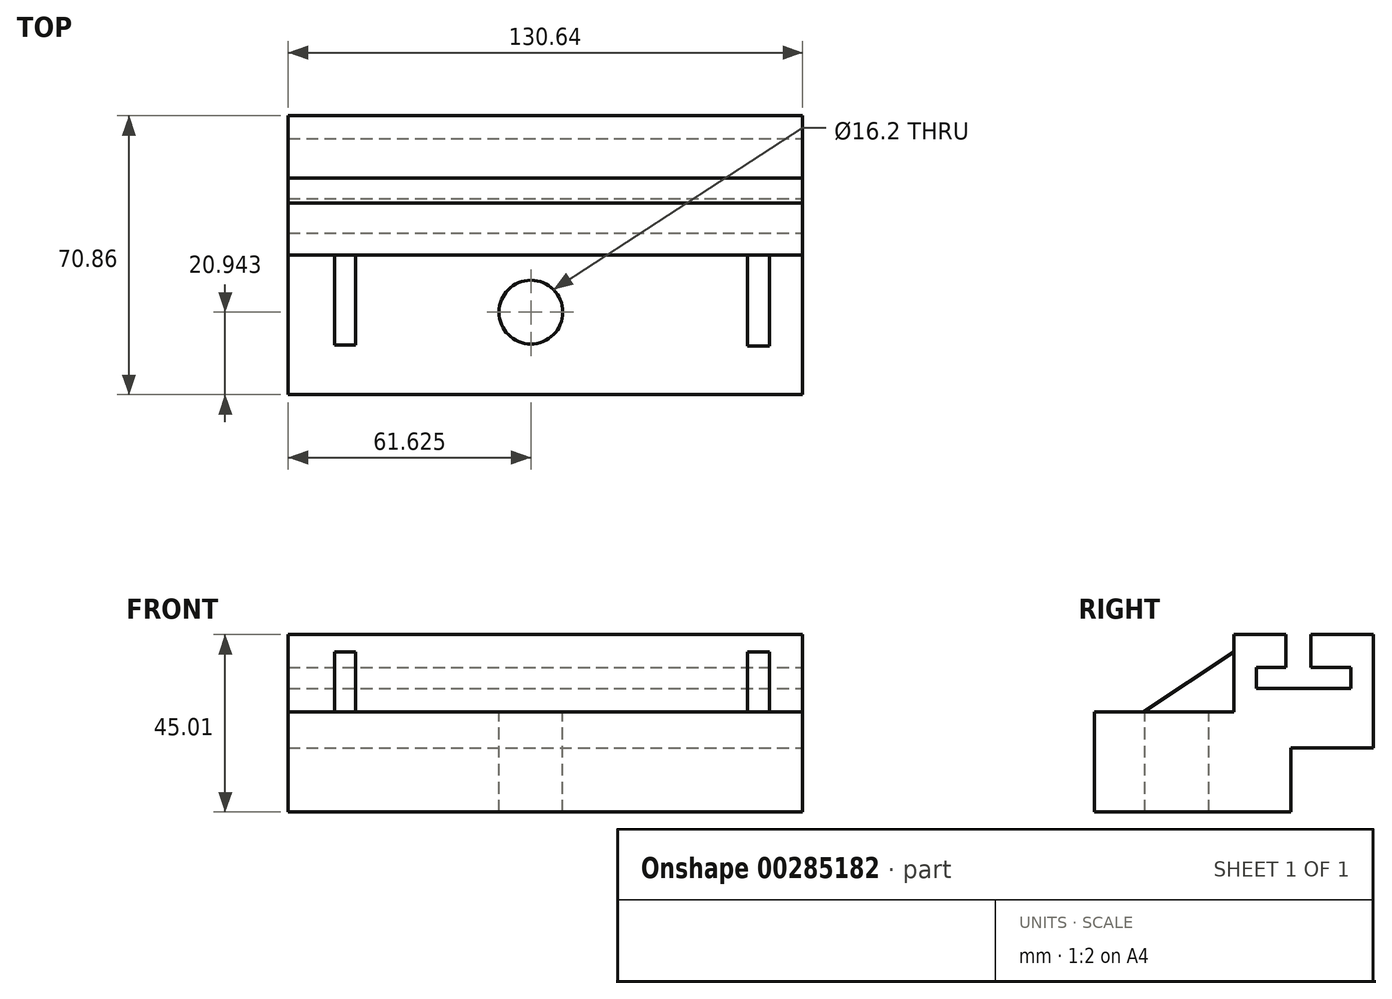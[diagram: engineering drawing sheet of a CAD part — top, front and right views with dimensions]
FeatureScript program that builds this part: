
annotation { "Feature Type Name" : "Feature", "Feature Type Description" : "" }
export const myFeature = defineFeature(function(context is Context, id is Id, definition is map)
    precondition{}
    {
        {
            var Q0;
            Q0=qCreatedBy(makeId("Top.planeOp"),FACE);
            var sketch = newSketch(context, id + "F0", { "sketchPlane" : qUnion([Q0])});
            skLineSegment(sketch, "E0.bottom", {"start": v(-58.77, 27.96) * mm, "end": v(71.87, 27.96) * mm});
            skLineSegment(sketch, "E0.top", {"start": v(-58.77, -42.9) * mm, "end": v(71.87, -42.9) * mm});
            skLineSegment(sketch, "E0.left", {"start": v(-58.77, 27.96) * mm, "end": v(-58.77, -42.9) * mm});
            skLineSegment(sketch, "E0.right", {"start": v(71.87, 27.96) * mm, "end": v(71.87, -42.9) * mm});
            skSolve(sketch);
        }
        {
            var Q0;
            Q0=makeQuery(id+"F0.imprint","IMPRINT",FACE,{"disambiguationData":[TD([[makeQuery(id+"F0.imprint","IMPRINT",EDGE,{"derivedFrom":sQuery(id+"F0.wireOp",EDGE,"E0.bottom")}),-1.0]])]});
            extrude(context, id + "F1", {"entities" : qUnion([Q0]), "depth" : 25.4 * mm});
        }
        {
            var Q0;
            Q0=makeQuery(id+"F1.opExtrude","SWEPT_FACE",FACE,{"disambiguationData":[OSD([sQuery(id+"F0.wireOp",EDGE,"E0.right")])]});
            var sketch = newSketch(context, id + "F2", { "sketchPlane" : qUnion([Q0])});
            skLineSegment(sketch, "E1.bottom", {"start": v(6.95, 0) * mm, "end": v(27.96, 0) * mm});
            skLineSegment(sketch, "E1.top", {"start": v(6.95, 16.2) * mm, "end": v(27.96, 16.2) * mm});
            skLineSegment(sketch, "E1.left", {"start": v(6.95, 0) * mm, "end": v(6.95, 16.2) * mm});
            skLineSegment(sketch, "E1.right", {"start": v(27.96, 0) * mm, "end": v(27.96, 16.2) * mm});
            skSolve(sketch);
        }
        {
            var Q0;
            Q0=makeQuery(id+"F2.imprint","IMPRINT",FACE,{"disambiguationData":[TD([[makeQuery(id+"F2.imprint","IMPRINT",EDGE,{"derivedFrom":sQuery(id+"F2.wireOp",EDGE,"E1.bottom")}),-1.0]])]});
            extrude(context, id + "F3", {"entities" : qUnion([Q0]), "operationType" : NewBodyOperationType.REMOVE, "oppositeDirection" : true, "depth" : 139.7 * mm});
        }
        {
            var Q0;
            Q0=makeQuery(id+"F1.opExtrude","CAP_FACE",FACE,{"disambiguationData":[OSD([sQuery(id+"F0.wireOp",EDGE,"E0.bottom"),sQuery(id+"F0.wireOp",EDGE,"E0.top"),sQuery(id+"F0.wireOp",EDGE,"E0.left"),sQuery(id+"F0.wireOp",EDGE,"E0.right")])],"isStart":false});
            var sketch = newSketch(context, id + "F4", { "sketchPlane" : qUnion([Q0])});
            skLineSegment(sketch, "E2.bottom", {"start": v(-58.77, 27.96) * mm, "end": v(71.87, 27.96) * mm});
            skLineSegment(sketch, "E2.top", {"start": v(-58.77, -7.47) * mm, "end": v(71.87, -7.47) * mm});
            skLineSegment(sketch, "E2.left", {"start": v(-58.77, 27.96) * mm, "end": v(-58.77, -7.47) * mm});
            skLineSegment(sketch, "E2.right", {"start": v(71.87, 27.96) * mm, "end": v(71.87, -7.47) * mm});
            skSolve(sketch);
        }
        {
            var Q0;
            Q0=makeQuery(id+"F4.imprint","IMPRINT",FACE,{"disambiguationData":[TD([[makeQuery(id+"F4.imprint","IMPRINT",EDGE,{"derivedFrom":sQuery(id+"F4.wireOp",EDGE,"E2.bottom")}),-1.0]])]});
            extrude(context, id + "F5", {"entities" : qUnion([Q0]), "operationType" : NewBodyOperationType.ADD, "depth" : 27.94 * mm});
        }
        {
            var Q0;
            Q0=makeQuery(id+"F5.boolean.opBoolean","MERGE",FACE,{"derivedFrom":[makeQuery(id+"F1.opExtrude","SWEPT_FACE",FACE,{"disambiguationData":[OSD([sQuery(id+"F0.wireOp",EDGE,"E0.right")])]}),makeQuery(id+"F5.opExtrude","SWEPT_FACE",FACE,{"disambiguationData":[OSD([sQuery(id+"F4.wireOp",EDGE,"E2.right")])]})]});
            var sketch = newSketch(context, id + "F6", { "sketchPlane" : qUnion([Q0])});
            skLineSegment(sketch, "E3", {"start": v(5.7, 53.34) * mm, "end": v(5.7, 36.69) * mm});
            skLineSegment(sketch, "E4", {"start": v(5.7, 36.69) * mm, "end": v(-1.85, 36.69) * mm});
            skLineSegment(sketch, "E5", {"start": v(-1.85, 36.69) * mm, "end": v(-1.85, 31.32) * mm});
            skLineSegment(sketch, "E6", {"start": v(-1.85, 31.32) * mm, "end": v(22.16, 31.32) * mm});
            skLineSegment(sketch, "E7", {"start": v(22.16, 36.69) * mm, "end": v(22.16, 31.32) * mm});
            skLineSegment(sketch, "E8", {"start": v(22.16, 36.69) * mm, "end": v(12.09, 36.69) * mm});
            skLineSegment(sketch, "E9", {"start": v(12.09, 36.69) * mm, "end": v(12.09, 53.34) * mm});
            skSolve(sketch);
        }
        {
            var Q0;
            {var subQ0=sQuery(id+"F6.wireOp",EDGE,"E3");Q0=makeQuery(id+"F6.imprint","IMPRINT",FACE,{"disambiguationData":[TD([[makeQuery(id+"F6.imprint","IMPRINT",EDGE,{"derivedFrom":subQ0}),1.0]])]});}
            extrude(context, id + "F7", {"entities" : qUnion([Q0]), "operationType" : NewBodyOperationType.REMOVE, "oppositeDirection" : true, "depth" : 157.48 * mm});
        }
        {
            var Q0;
            Q0=makeQuery(id+"F5.boolean.opBoolean","MERGE",FACE,{"derivedFrom":[makeQuery(id+"F1.opExtrude","SWEPT_FACE",FACE,{"disambiguationData":[OSD([sQuery(id+"F0.wireOp",EDGE,"E0.right")])]}),makeQuery(id+"F5.opExtrude","SWEPT_FACE",FACE,{"disambiguationData":[OSD([sQuery(id+"F4.wireOp",EDGE,"E2.right")])]})]});
            var sketch = newSketch(context, id + "F8", { "sketchPlane" : qUnion([Q0])});
            skLineSegment(sketch, "E10.bottom", {"start": v(-7.47, 53.34) * mm, "end": v(5.7, 53.34) * mm});
            skLineSegment(sketch, "E10.top", {"start": v(-7.47, 45.01) * mm, "end": v(5.7, 45.01) * mm});
            skLineSegment(sketch, "E10.left", {"start": v(-7.47, 53.34) * mm, "end": v(-7.47, 45.01) * mm});
            skLineSegment(sketch, "E10.right", {"start": v(5.7, 53.34) * mm, "end": v(5.7, 45.01) * mm});
            skPoint(sketch, "E11.oppositeSnap0", {"position": v(12.09, 45.01) * mm});
            skLineSegment(sketch, "E11.bottom", {"start": v(12.09, 53.34) * mm, "end": v(27.96, 53.34) * mm});
            skLineSegment(sketch, "E11.top", {"start": v(12.09, 45.01) * mm, "end": v(27.96, 45.01) * mm});
            skLineSegment(sketch, "E11.left", {"start": v(12.09, 53.34) * mm, "end": v(12.09, 45.01) * mm});
            skLineSegment(sketch, "E11.right", {"start": v(27.96, 53.34) * mm, "end": v(27.96, 45.01) * mm});
            skSolve(sketch);
        }
        {
            var Q0;
            Q0=makeQuery(id+"F8.imprint","IMPRINT",FACE,{"disambiguationData":[TD([[makeQuery(id+"F8.imprint","IMPRINT",EDGE,{"derivedFrom":sQuery(id+"F8.wireOp",EDGE,"E10.bottom")}),1.0]])]});
            var Q1;
            Q1=makeQuery(id+"F8.imprint","IMPRINT",FACE,{"disambiguationData":[TD([[makeQuery(id+"F8.imprint","IMPRINT",EDGE,{"derivedFrom":sQuery(id+"F8.wireOp",EDGE,"E11.bottom")}),1.0]])]});
            extrude(context, id + "F9", {"entities" : qUnion([Q0, Q1]), "operationType" : NewBodyOperationType.REMOVE, "oppositeDirection" : true, "depth" : 147.32 * mm});
        }
        {
            var Q0;
            Q0=makeQuery(id+"F1.opExtrude","CAP_FACE",FACE,{"disambiguationData":[OSD([sQuery(id+"F0.wireOp",EDGE,"E0.bottom"),sQuery(id+"F0.wireOp",EDGE,"E0.top"),sQuery(id+"F0.wireOp",EDGE,"E0.left"),sQuery(id+"F0.wireOp",EDGE,"E0.right")])],"isStart":false});
            var sketch = newSketch(context, id + "F10", { "sketchPlane" : qUnion([Q0])});
            skLineSegment(sketch, "E12.bottom", {"start": v(-47.02, -7.47) * mm, "end": v(-41.64, -7.47) * mm});
            skLineSegment(sketch, "E12.top", {"start": v(-47.02, -30.27) * mm, "end": v(-41.64, -30.27) * mm});
            skLineSegment(sketch, "E12.left", {"start": v(-47.02, -7.47) * mm, "end": v(-47.02, -30.27) * mm});
            skLineSegment(sketch, "E12.right", {"start": v(-41.64, -7.47) * mm, "end": v(-41.64, -30.27) * mm});
            skSolve(sketch);
        }
        {
            var Q0;
            Q0=makeQuery(id+"F10.imprint","IMPRINT",FACE,{"disambiguationData":[TD([[makeQuery(id+"F10.imprint","IMPRINT",EDGE,{"derivedFrom":sQuery(id+"F10.wireOp",EDGE,"E12.bottom")}),-1.0]])]});
            extrude(context, id + "F11", {"entities" : qUnion([Q0]), "operationType" : NewBodyOperationType.ADD, "depth" : 15.24 * mm});
        }
        {
            var Q0;
            Q0=makeQuery(id+"F11.opExtrude","SWEPT_FACE",FACE,{"disambiguationData":[OSD([sQuery(id+"F10.wireOp",EDGE,"E12.left")])]});
            var sketch = newSketch(context, id + "F12", { "sketchPlane" : qUnion([Q0])});
            skLineSegment(sketch, "E13", {"start": v(7.47, 40.64) * mm, "end": v(30.27, 25.4) * mm});
            skSolve(sketch);
        }
        {
            var Q0;
            Q0=makeQuery(id+"F12.imprint","IMPRINT",FACE,{"disambiguationData":[TD([[makeQuery(id+"F12.imprint","IMPRINT",EDGE,{"derivedFrom":sQuery(id+"F12.wireOp",EDGE,"E13")}),1.0]])]});
            extrude(context, id + "F13", {"entities" : qUnion([Q0]), "operationType" : NewBodyOperationType.REMOVE, "oppositeDirection" : true, "depth" : 25.4 * mm});
        }
        {
            var Q0;
            Q0=makeQuery(id+"F1.opExtrude","CAP_FACE",FACE,{"disambiguationData":[OSD([sQuery(id+"F0.wireOp",EDGE,"E0.bottom"),sQuery(id+"F0.wireOp",EDGE,"E0.top"),sQuery(id+"F0.wireOp",EDGE,"E0.left"),sQuery(id+"F0.wireOp",EDGE,"E0.right")])],"isStart":false});
            var sketch = newSketch(context, id + "F14", { "sketchPlane" : qUnion([Q0])});
            skLineSegment(sketch, "E14.bottom", {"start": v(57.93, -7.47) * mm, "end": v(63.47, -7.47) * mm});
            skLineSegment(sketch, "E14.top", {"start": v(57.93, -30.5) * mm, "end": v(63.47, -30.5) * mm});
            skLineSegment(sketch, "E14.left", {"start": v(57.93, -7.47) * mm, "end": v(57.93, -30.5) * mm});
            skLineSegment(sketch, "E14.right", {"start": v(63.47, -7.47) * mm, "end": v(63.47, -30.5) * mm});
            skSolve(sketch);
        }
        {
            var Q0;
            Q0=makeQuery(id+"F14.imprint","IMPRINT",FACE,{"disambiguationData":[TD([[makeQuery(id+"F14.imprint","IMPRINT",EDGE,{"derivedFrom":sQuery(id+"F14.wireOp",EDGE,"E14.bottom")}),-1.0]])]});
            extrude(context, id + "F15", {"entities" : qUnion([Q0]), "operationType" : NewBodyOperationType.ADD, "depth" : 15.24 * mm});
        }
        {
            var Q0;
            Q0=makeQuery(id+"F15.opExtrude","SWEPT_FACE",FACE,{"disambiguationData":[OSD([sQuery(id+"F14.wireOp",EDGE,"E14.left")])]});
            var sketch = newSketch(context, id + "F16", { "sketchPlane" : qUnion([Q0])});
            skLineSegment(sketch, "E15", {"start": v(7.47, 40.64) * mm, "end": v(30.5, 25.4) * mm});
            skSolve(sketch);
        }
        {
            var Q0;
            Q0=makeQuery(id+"F16.imprint","IMPRINT",FACE,{"disambiguationData":[TD([[makeQuery(id+"F16.imprint","IMPRINT",EDGE,{"derivedFrom":sQuery(id+"F16.wireOp",EDGE,"E15")}),1.0]])]});
            extrude(context, id + "F17", {"entities" : qUnion([Q0]), "operationType" : NewBodyOperationType.REMOVE, "oppositeDirection" : true, "depth" : 25.4 * mm});
        }
        {
            var Q0;
            Q0=makeQuery(id+"F1.opExtrude","CAP_FACE",FACE,{"disambiguationData":[OSD([sQuery(id+"F0.wireOp",EDGE,"E0.bottom"),sQuery(id+"F0.wireOp",EDGE,"E0.top"),sQuery(id+"F0.wireOp",EDGE,"E0.left"),sQuery(id+"F0.wireOp",EDGE,"E0.right")])],"isStart":false});
            var sketch = newSketch(context, id + "F18", { "sketchPlane" : qUnion([Q0])});
            skLineSegment(sketch, "E16", {"start": v(2.85, -21.96) * mm, "end": v(2.85, -7.47) * mm});
            skLineSegment(sketch, "E17", {"start": v(2.85, -21.96) * mm, "end": v(2.85, -33.36) * mm});
            skLineSegment(sketch, "E18", {"start": v(2.85, -21.96) * mm, "end": v(-8.73, -21.96) * mm});
            skLineSegment(sketch, "E19", {"start": v(2.85, -21.96) * mm, "end": v(13.43, -21.96) * mm});
            skCircle(sketch, "E20", {"center": v(2.85, -21.96) * mm, "radius": 8.1 * mm});
            skSolve(sketch);
        }
        {
            var Q0;
            {var subQ1=sQuery(id+"F18.wireOp",EDGE,"E16");var subQ3=sQuery(id+"F18.wireOp",EDGE,"E20");var subQ4=makeQuery(id+"F18.imprint","INTERSECT",VERTEX,{"derivedFrom":[subQ1,subQ3]});Q0=makeQuery(id+"F18.imprint","IMPRINT",FACE,{"disambiguationData":[TD([[makeQuery(id+"F18.imprint","IMPRINT",EDGE,{"disambiguationData":[TD([[subQ4,-1.0]])],"derivedFrom":subQ3}),1.0]])]});}
            var Q1;
            {var subQ1=sQuery(id+"F18.wireOp",EDGE,"E16");var subQ3=sQuery(id+"F18.wireOp",EDGE,"E20");var subQ4=makeQuery(id+"F18.imprint","INTERSECT",VERTEX,{"derivedFrom":[subQ1,subQ3]});Q1=makeQuery(id+"F18.imprint","IMPRINT",FACE,{"disambiguationData":[TD([[makeQuery(id+"F18.imprint","IMPRINT",EDGE,{"disambiguationData":[TD([[subQ4,1.0]])],"derivedFrom":subQ3}),1.0]])]});}
            var Q2;
            {var subQ1=sQuery(id+"F18.wireOp",EDGE,"E17");var subQ3=sQuery(id+"F18.wireOp",EDGE,"E20");var subQ4=makeQuery(id+"F18.imprint","INTERSECT",VERTEX,{"derivedFrom":[subQ1,subQ3]});Q2=makeQuery(id+"F18.imprint","IMPRINT",FACE,{"disambiguationData":[TD([[makeQuery(id+"F18.imprint","IMPRINT",EDGE,{"disambiguationData":[TD([[subQ4,1.0]])],"derivedFrom":subQ3}),1.0]])]});}
            var Q3;
            {var subQ1=sQuery(id+"F18.wireOp",EDGE,"E17");var subQ3=sQuery(id+"F18.wireOp",EDGE,"E20");var subQ4=makeQuery(id+"F18.imprint","INTERSECT",VERTEX,{"derivedFrom":[subQ1,subQ3]});Q3=makeQuery(id+"F18.imprint","IMPRINT",FACE,{"disambiguationData":[TD([[makeQuery(id+"F18.imprint","IMPRINT",EDGE,{"disambiguationData":[TD([[subQ4,-1.0]])],"derivedFrom":subQ3}),1.0]])]});}
            extrude(context, id + "F19", {"entities" : qUnion([Q0, Q1, Q2, Q3]), "operationType" : NewBodyOperationType.REMOVE, "oppositeDirection" : true, "depth" : 45.72 * mm});
        }
    });
